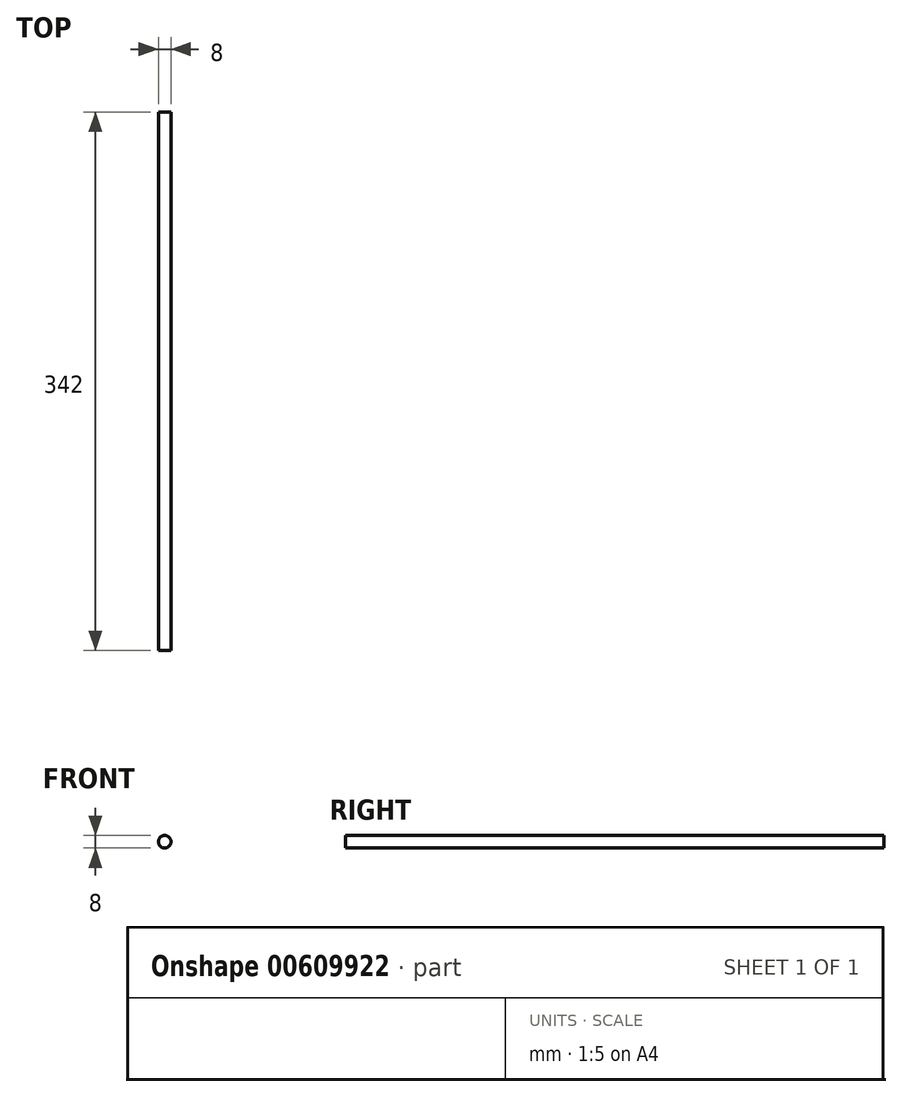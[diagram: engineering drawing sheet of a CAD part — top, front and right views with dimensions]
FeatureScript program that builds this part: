
annotation { "Feature Type Name" : "Feature", "Feature Type Description" : "" }
export const myFeature = defineFeature(function(context is Context, id is Id, definition is map)
    precondition{}
    {
        {
            var Q0;
            Q0=qCreatedBy(makeId("Front.planeOp"),FACE);
            var sketch = newSketch(context, id + "F0", { "sketchPlane" : qUnion([Q0])});
            skCircle(sketch, "E0", {"center": v(0, 0) * mm, "radius": 4 * mm});
            skSolve(sketch);
        }
        {
            var Q0;
            Q0 = qSketchRegion(id + "F0", true);
            extrude(context, id + "F1", {"entities" : qUnion([Q0]), "depth" : 342 * mm, "offsetDistance" : 25 * mm, "symmetric" : true});
        }
    });
